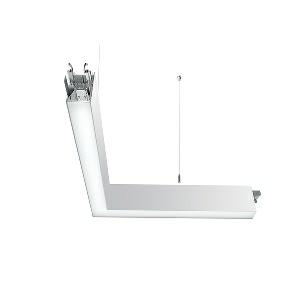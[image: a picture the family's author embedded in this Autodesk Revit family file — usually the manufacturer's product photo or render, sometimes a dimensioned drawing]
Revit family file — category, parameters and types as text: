
# Revit family: dotoo_line_-_dlp_1500_830_d_lr_mid_00807695_5251
name_source: partatom
category: Lighting Fixtures
units: mm (PartAtom-declared; Revit-internal decimal feet)

## family parameters
Cut with Voids When Loaded = No
Host = Face
Light Source = No
Part Type = Normal
Room Calculation Point = No
Round Connector Dimension = Use Diameter
Shared = No

## types (1)
- DOTOO.line - DLP 1500/830/D/LR MID (1 x LED, 1300 lm, 3000K)
    Apparent Load = 13 VA
    Approval mark = CE
    CIE Flux Codes = 67 91 98 100 100
    Color Rendering = 80-89
    Color Temperature = 3000K
    Control Gear = Electronic ballast
    Default Elevation = 1800 mm
    Description = DLP 1500/830/D|Suspended luminaire|light source: LED|connected load: 220-240 V, 50/60 Hz|Power consumption: approx. 13 W|standby: approx. 0,20|luminous flux: 1300 lm|luminous efficacy: 100 lm/W|light distribution: Direct|direct ratio: approx. 100 %|colour temperature: Warm white, ca. 3000 K|color rendering index (CRI): >= 80|chromaticity tolerance:  3 SDCM|System of protection: IP 40|technology: Continuously dimmable|luminaire body|material: Sectional aluminium|colour: White|lamp cover: Acrylic (PMMA), Clear|Fastening: Steel cable 0.3 - 0.7 m|glare control: Prism aperture|luminance(L65): <= 3000 cd/m|unified glare rating(4H 8H): <=  19|special features: DALI Load 1x, TouchDIM - dimming via standard switch, Through-wired, up to 18 m on one mains connection, Flicker-free, Continous light without dark z, Suitable as emergency lighting, 90░ rerouting on the right sid, Mechanical and electrical connection of the individual modules without tools|
    Frequency = 50 Hz
    Height = 110 mm
    Lamp = 1 x LED
    Lamp Light Flux = 1300 lm
    Lamp count = 1
    Length = 600 mm
    Luminous efficacy = 100 lm/W
    Manufacturer = Waldmann
    ModVariant = No
    Model = 00807695
    Mounting Place = Ceiling
    Mounting Type = Pendant
    Number of Poles = 1
    OnlyDefault = Yes
    Power Factor = 1
    Product Name = DOTOO.line - DLP 1500/830/D/LR MID
    Product group = Suspended luminaire
    ProductGroupID = 9
    Protection Class = Protection class I
    Protection Degree = IP 40
    RLX_Detail_Level = 1
    RLX_Emergency_Light_Flux = 0 lm
    RLX_Emergency_Type = 0
    RLX_Emergency_Type_DB = No
    RlxData = <blob elided: 21205 chars, md5=3f894acf>
    Socket = socket
    Standby Power = 0 W
    System Light Flux = 1300 lm
    System Power = 13 W
    Type Comments = Product without accessories
    Type Image = ilp_dlp_lr_ws.jpg
    URL = http://relux.com
    VarID = ---
    Voltage = 230 V
    Voltage Range = 220-240 V
    Weight = 0.00 kg
    Width = 600 mm

## geometry (parser evidence)
native form markers: Blend x4, Sweep x12
no freeform markers — native parametric forms only
